# Revit family: SANINDUSA_140034004_Urb.y_Urb.y48RimFlushWallMountedToiletWConcealedFixation350x483x330_V0
name_source: partatom
category: Plumbing Fixtures
units: mm (PartAtom-declared; Revit-internal decimal feet)

## family parameters
Cut with Voids When Loaded = No
Host = Face
Part Type = Normal
Room Calculation Point = No
Round Connector Dimension = Use Diameter
Shared = No

## types (1)
- SANINDUSA_140034004_Urb.y_Urb.y48RimFlushWallMountedToiletWConcealedFixation350x483x330_V0
    AssetType = Fixed
    CodePerformance = EN 997:2012  CL 1 - 6 A
    Color = white
    Constituents = Compatible toilet seats (not included): 24011 ‐ Urb.y clipOff toilet seat; 24031 ‐ Urb.y clipOff slowclose toilet seat; 41733xx ‐ SANGLASS WALL external frame w/ dual flushing cistern for; wall hung WC; 4193311 ‐ SANSLIM build‐in element w/dual flushing cistern and To‐slim; plate for wall hung WC; 40333 ‐ SANFIX frame w/ dual flushing cistern for wall hung WC; (for brick walls); 4103311 ‐ Moove 3/6Lt mechanism plate; 40333 ‐ SANFIX frame w/ dual flushing cistern for wall hung WC; (for brick walls); 40323 ‐ Free standing SANFIX frame w/ dual flushing cistern for wall hung WC; 40233 ‐ SANFLUSH build‐in element w/ dual flushing cistern for wall hung WC; 40633 ‐ SANSPACE frame w/ dual flushing cistern for wall hung WC; (for brick walls); 40533 ‐ SANBEST build‐in element w/ dual flushing cistern for wall (for brick walls)
    Default Elevation = 1219 mm
    Description = Soil appliance for the disposal of excrement.
    DrainSize = 100 mm  [stored 0.328084 ft]
    Element Type = TOILETPAN: Soil appliance for the disposal of excrement.
    Features = "Domestic and commercial use. With rimflush discharge system without rim, which promotes hygiene,
make easier the toilet cleaning and reduces the proliferation of germs. Toilet seat with clipoff system easy to clean and slow close. Without holes in the sidewalls. Invisible fixation"
    Finish = gloss
    InletDiameter = 0 mm  [stored 0 ft]
    Installation Instructions = https://www.tec.sanindusa.pt
    Manufacturer = Sanindusa
    ManufacturerName = Sanindusa
    ManufacturerURL = www.tec.sanindusa.pt
    Material = vitreous china
    Model = 140034004
    ModelNumber = 140034004
    ModelReference = Urb.y
    Name = Urb.y 48 rimflush wall mounted wc
    NominalHeight = 330 mm
    NominalLength = 350 mm  [stored 1.14829 ft]
    NominalWidth = 483 mm
    PanColor = white
    PanMaterial = vitreous china
    PanMounting = wallhung
    Pre-defined type (IFC) = TOILETPAN
    ProductInformation = https://www.tec.sanindusa.pt
    ProductionYear = 2017
    Size = 350x483x330
    ToiletPanType = washdown
washdown
washdown
    ToiletType = LooseCoupled
    Type (IFC) = IfcSanitaryTerminalType
    URL = www.tec.sanindusa.pt
    Version = 1
    WarrantyDescription = https://www.tec.sanindusa.pt
    WarrantyDurationParts = 5
    WarrantyDurationUnit = year
    Waste Connection = Yes
    Weight = 18.80 kg

note: [stored X ft] marks values corroborated as IEEE doubles in the binary element streams (Revit-internal decimal feet)

## geometry (parser evidence)
native form markers: Sweep x8
no freeform markers — native parametric forms only
